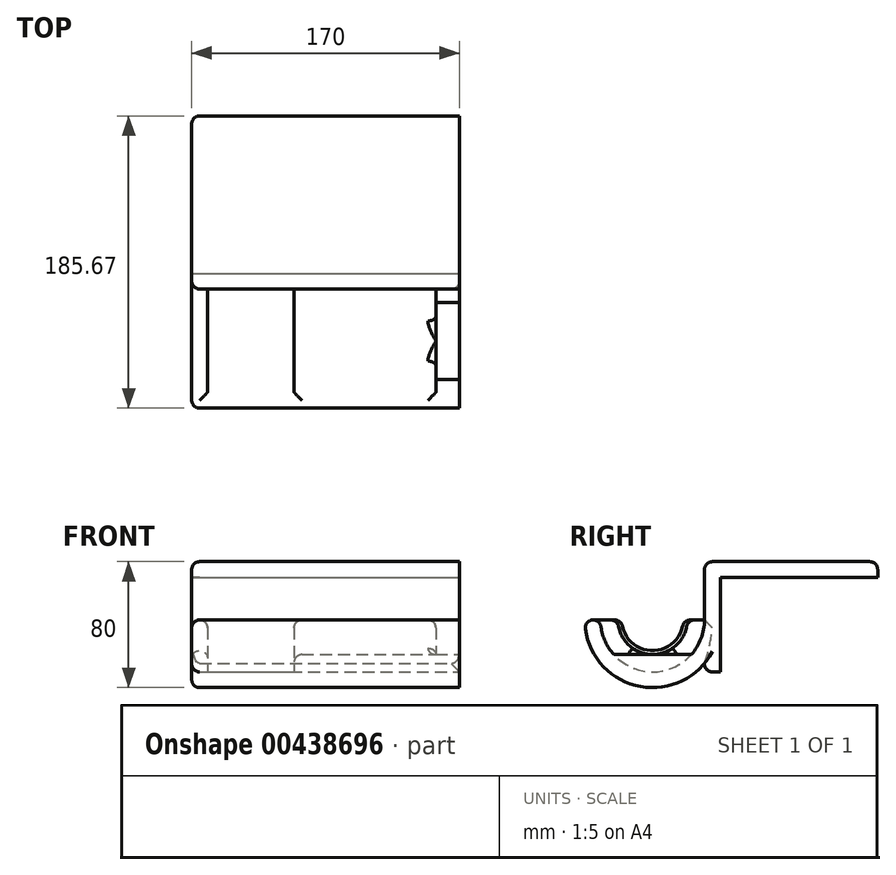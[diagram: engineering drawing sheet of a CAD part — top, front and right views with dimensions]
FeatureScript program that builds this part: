
annotation { "Feature Type Name" : "Feature", "Feature Type Description" : "" }
export const myFeature = defineFeature(function(context is Context, id is Id, definition is map)
    precondition{}
    {
        {
            var Q0;
            Q0=qCreatedBy(makeId("Front.planeOp"),FACE);
            var sketch = newSketch(context, id + "F0", { "sketchPlane" : qUnion([Q0])});
            skLineSegment(sketch, "E0.bottom", {"start": v(-170, 10) * mm, "end": v(170, 10) * mm});
            skLineSegment(sketch, "E0.top", {"start": v(-170, -60) * mm, "end": v(170, -60) * mm});
            skLineSegment(sketch, "E0.left", {"start": v(-170, 10) * mm, "end": v(-170, -60) * mm});
            skLineSegment(sketch, "E0.right", {"start": v(170, 10) * mm, "end": v(170, -60) * mm});
            skSolve(sketch);
        }
        {
            var Q0;
            Q0=qSketchRegion(id+"F0",true);
            extrude(context, id + "F1", {"entities" : qUnion([Q0]), "depth" : 10 * mm});
        }
        {
            var Q0;
            Q0=qCreatedBy(makeId("Top.planeOp"),FACE);
            var sketch = newSketch(context, id + "F2", { "sketchPlane" : qUnion([Q0])});
            skLineSegment(sketch, "E1.bottom", {"start": v(-170, 0) * mm, "end": v(170, 0) * mm});
            skLineSegment(sketch, "E1.top", {"start": v(-170, 100) * mm, "end": v(170, 100) * mm});
            skLineSegment(sketch, "E1.left", {"start": v(-170, 0) * mm, "end": v(-170, 100) * mm});
            skLineSegment(sketch, "E1.right", {"start": v(170, 0) * mm, "end": v(170, 100) * mm});
            skSolve(sketch);
        }
        {
            var Q0;
            Q0=qSketchRegion(id+"F2",true);
            extrude(context, id + "F3", {"entities" : qUnion([Q0]), "operationType" : NewBodyOperationType.ADD, "depth" : 10 * mm});
        }
        {
            var Q0;
            Q0=qCreatedBy(makeId("Top.planeOp"),FACE);
            cPlane(context, id + "F4", {"entities" : qUnion([Q0]), "cplaneType" : CPlaneType.OFFSET, "offset" : 27 * mm, "oppositeDirection" : true, "width" : 150 * mm, "height" : 150 * mm});
        }
        {
            var Q0;
            Q0=qCreatedBy(id+"F4.planeOp",FACE);
            var sketch = newSketch(context, id + "F5", { "sketchPlane" : qUnion([Q0])});
            skLineSegment(sketch, "E2", {"start": v(-170, 0) * mm, "end": v(-170, -43) * mm});
            skLineSegment(sketch, "E3", {"start": v(-170, -43) * mm, "end": v(-160, -43) * mm});
            skLineSegment(sketch, "E4", {"start": v(-160, -43) * mm, "end": v(-160, -10) * mm});
            skLineSegment(sketch, "E5", {"start": v(-160, -10) * mm, "end": v(-105, -10) * mm});
            skLineSegment(sketch, "E6", {"start": v(-105, -10) * mm, "end": v(-105, -21) * mm});
            skLineSegment(sketch, "E7", {"start": v(-105, -21) * mm, "end": v(-15, -21) * mm});
            skLineSegment(sketch, "E8", {"start": v(-15, -21) * mm, "end": v(-15, -10) * mm});
            skLineSegment(sketch, "E9", {"start": v(-15, -10) * mm, "end": v(52.5, -10) * mm});
            skLineSegment(sketch, "E10", {"start": v(52.5, -10) * mm, "end": v(52.5, -21) * mm});
            skLineSegment(sketch, "E11", {"start": v(52.5, -21) * mm, "end": v(105, -21) * mm});
            skLineSegment(sketch, "E12", {"start": v(105, -21) * mm, "end": v(105, -10) * mm});
            skLineSegment(sketch, "E13", {"start": v(105, -10) * mm, "end": v(160, -10) * mm});
            skLineSegment(sketch, "E14", {"start": v(160, -10) * mm, "end": v(160, -43) * mm});
            skLineSegment(sketch, "E15", {"start": v(160, -43) * mm, "end": v(170, -43) * mm});
            skLineSegment(sketch, "E16", {"start": v(170, -43) * mm, "end": v(170, 0) * mm});
            skLineSegment(sketch, "E17", {"start": v(170, 0) * mm, "end": v(-170, 0) * mm});
            skSolve(sketch);
        }
        {
            var Q0;
            Q0=qCreatedBy(id+"F4.planeOp",FACE);
            var sketch = newSketch(context, id + "F6", { "sketchPlane" : qUnion([Q0])});
            skLineSegment(sketch, "E18", {"start": v(170, -43) * mm, "end": v(-170, -43) * mm});
            skSolve(sketch);
        }
        {
            var Q0;
            Q0=qSketchRegion(id+"F5",true);
            var Q1;
            Q1=sQuery(id+"F6.wireOp",EDGE,"E18");
            revolve(context, id + "F7", {"operationType" : NewBodyOperationType.ADD, "entities" : qUnion([Q0]), "axis" : qUnion([Q1]), "revolveType" : RevolveType.ONE_DIRECTION, "angle" : 180 * degree});
        }
        {
            var Q0;
            Q0=qCreatedBy(makeId("Right.planeOp"),FACE);
            var sketch = newSketch(context, id + "F8", { "sketchPlane" : qUnion([Q0])});
            skCircle(sketch, "E19", {"center": v(-43, -27) * mm, "radius": 19.5 * mm});
            skSolve(sketch);
        }
        {
            var Q0;
            Q0=makeQuery(id+"F8.imprint","IMPRINT",FACE,{"disambiguationData":[TD([[makeQuery(id+"F8.imprint","IMPRINT",EDGE,{"derivedFrom":sQuery(id+"F8.wireOp",EDGE,"E19")}),1.0]])]});
            extrude(context, id + "F9", {"entities" : qUnion([Q0]), "operationType" : NewBodyOperationType.REMOVE, "endBound" : BoundingType.THROUGH_ALL, "depth" : 25 * mm});
        }
        {
            var Q0;
            Q0=qSketchRegion(id+"F8",true);
            extrude(context, id + "F10", {"entities" : qUnion([Q0]), "operationType" : NewBodyOperationType.REMOVE, "endBound" : BoundingType.THROUGH_ALL, "oppositeDirection" : true, "depth" : 25 * mm});
        }
        {
            var Q0;
            Q0=qCreatedBy(id+"F4.planeOp",FACE);
            cPlane(context, id + "F11", {"entities" : qUnion([Q0]), "cplaneType" : CPlaneType.OFFSET, "offset" : 22 * mm, "oppositeDirection" : true, "width" : 150 * mm, "height" : 150 * mm});
        }
        {
            var Q0;
            Q0=qCreatedBy(id+"F11.planeOp",FACE);
            var sketch = newSketch(context, id + "F12", { "sketchPlane" : qUnion([Q0])});
            skLineSegment(sketch, "E20.bottom", {"start": v(-15, -10) * mm, "end": v(52.5, -10) * mm});
            skLineSegment(sketch, "E20.top", {"start": v(-15, -76) * mm, "end": v(52.5, -76) * mm});
            skLineSegment(sketch, "E20.left", {"start": v(-15, -10) * mm, "end": v(-15, -76) * mm});
            skLineSegment(sketch, "E20.right", {"start": v(52.5, -10) * mm, "end": v(52.5, -76) * mm});
            skSolve(sketch);
        }
        {
            var Q0;
            Q0=makeQuery(id+"F12.imprint","IMPRINT",FACE,{"disambiguationData":[TD([[makeQuery(id+"F12.imprint","IMPRINT",EDGE,{"derivedFrom":sQuery(id+"F12.wireOp",EDGE,"E20.bottom")}),-1.0]])]});
            extrude(context, id + "F13", {"entities" : qUnion([Q0]), "operationType" : NewBodyOperationType.ADD, "oppositeDirection" : true, "depth" : 25 * mm});
        }
        {
            var Q0;
            Q0=makeQuery(id+"F13.opExtrude","SWEPT_FACE",FACE,{"disambiguationData":[OSD([sQuery(id+"F12.wireOp",EDGE,"E20.right")])]});
            var sketch = newSketch(context, id + "F14", { "sketchPlane" : qUnion([Q0])});
            skLineSegment(sketch, "E21", {"start": v(-76, -54.57) * mm, "end": v(-76, -74) * mm});
            skLineSegment(sketch, "E22", {"start": v(-76, -74) * mm, "end": v(-10, -74) * mm});
            skLineSegment(sketch, "E23", {"start": v(-10, -74) * mm, "end": v(-10, -54.57) * mm});
            skArc(sketch, "E24", {"start": v(-76, -54.57) * mm, "mid": v(-43, -70) * mm, "end": v(-10, -54.57) * mm});
            skSolve(sketch);
        }
        {
            var Q0;
            Q0=qSketchRegion(id+"F14",true);
            extrude(context, id + "F15", {"entities" : qUnion([Q0]), "operationType" : NewBodyOperationType.REMOVE, "endBound" : BoundingType.THROUGH_ALL, "oppositeDirection" : true, "depth" : 25 * mm});
        }
        {
            var Q0;
            Q0=qCreatedBy(makeId("Front.planeOp"),FACE);
            var sketch = newSketch(context, id + "F16", { "sketchPlane" : qUnion([Q0])});
            skLineSegment(sketch, "E25.bottom", {"start": v(0, 100) * mm, "end": v(200, 100) * mm});
            skLineSegment(sketch, "E25.top", {"start": v(0, -100) * mm, "end": v(200, -100) * mm});
            skLineSegment(sketch, "E25.left", {"start": v(0, 100) * mm, "end": v(0, -100) * mm});
            skLineSegment(sketch, "E25.right", {"start": v(200, 100) * mm, "end": v(200, -100) * mm});
            skSolve(sketch);
        }
        {
            var Q0;
            Q0 = qSketchRegion(id + "F16", true);
            extrude(context, id + "F17", {"entities" : qUnion([Q0]), "operationType" : NewBodyOperationType.REMOVE, "endBound" : BoundingType.THROUGH_ALL, "oppositeDirection" : true, "depth" : 25 * mm});
        }
        {
            var Q0;
            Q0 = qSketchRegion(id + "F16", true);
            extrude(context, id + "F18", {"entities" : qUnion([Q0]), "operationType" : NewBodyOperationType.REMOVE, "endBound" : BoundingType.THROUGH_ALL, "depth" : 25 * mm});
        }
        {
            var Q0;
            Q0=makeQuery(id+"F7.opRevolve","CAP_EDGE",EDGE,{"disambiguationData":[OSD([sQuery(id+"F5.wireOp",EDGE,"E17")])],"isStart":false});
            var Q1;
            Q1=makeQuery(id+"F7.opRevolve","CAP_EDGE",EDGE,{"disambiguationData":[OSD([sQuery(id+"F5.wireOp",EDGE,"E9")])],"isStart":false});
            var Q2;
            Q2=makeQuery(id+"F13.boolean.opBoolean","SPLIT",EDGE,{"disambiguationData":[OD(1.0)],"derivedFrom":makeQuery(id+"F7.opRevolve","SWEPT_EDGE",EDGE,{"disambiguationData":[OSD([sQuery(id+"F5.wireOp",EDGE,"E7"),sQuery(id+"F5.wireOp",EDGE,"E8")])]})});
            var Q3;
            Q3=makeQuery(id+"F7.opRevolve","CAP_EDGE",EDGE,{"disambiguationData":[OSD([sQuery(id+"F5.wireOp",EDGE,"E8")])],"isStart":true});
            var Q4;
            Q4=makeQuery(id+"F7.opRevolve","CAP_EDGE",EDGE,{"disambiguationData":[OSD([sQuery(id+"F5.wireOp",EDGE,"E7")])],"isStart":true});
            var Q5;
            Q5=makeQuery(id+"F7.opRevolve","CAP_EDGE",EDGE,{"disambiguationData":[OSD([sQuery(id+"F5.wireOp",EDGE,"E7")])],"isStart":false});
            var Q6;
            Q6=makeQuery(id+"F7.opRevolve","CAP_EDGE",EDGE,{"disambiguationData":[OSD([sQuery(id+"F5.wireOp",EDGE,"E8")])],"isStart":false});
            var Q7;
            Q7=makeQuery(id+"F7.opRevolve","CAP_EDGE",EDGE,{"disambiguationData":[OSD([sQuery(id+"F5.wireOp",EDGE,"E6")])],"isStart":false});
            var Q8;
            Q8=makeQuery(id+"F7.opRevolve","CAP_EDGE",EDGE,{"disambiguationData":[OSD([sQuery(id+"F5.wireOp",EDGE,"E6")])],"isStart":true});
            var Q9;
            Q9=makeQuery(id+"F7.opRevolve","SWEPT_EDGE",EDGE,{"disambiguationData":[OSD([sQuery(id+"F5.wireOp",EDGE,"E6"),sQuery(id+"F5.wireOp",EDGE,"E7")])]});
            var Q10;
            Q10=makeQuery(id+"F10.boolean.opBoolean","INTERSECT",EDGE,{"derivedFrom":[makeQuery(id+"F7.opRevolve","SWEPT_FACE",FACE,{"disambiguationData":[OSD([sQuery(id+"F5.wireOp",EDGE,"E4")])]}),makeQuery(id+"F10.opExtrude","SWEPT_FACE",FACE,{"disambiguationData":[OSD([sQuery(id+"F8.wireOp",EDGE,"E19")])]})]});
            var Q11;
            Q11=makeQuery(id+"F10.boolean.opBoolean","INTERSECT",EDGE,{"derivedFrom":[makeQuery(id+"F7.boolean.opBoolean","MERGE",FACE,{"derivedFrom":[makeQuery(id+"F3.boolean.opBoolean","MERGE",FACE,{"derivedFrom":[makeQuery(id+"F1.opExtrude","SWEPT_FACE",FACE,{"disambiguationData":[OSD([sQuery(id+"F0.wireOp",EDGE,"E0.left")])]}),makeQuery(id+"F3.opExtrude","SWEPT_FACE",FACE,{"disambiguationData":[OSD([sQuery(id+"F2.wireOp",EDGE,"E1.left")])]})]}),makeQuery(id+"F7.opRevolve","SWEPT_FACE",FACE,{"disambiguationData":[OSD([sQuery(id+"F5.wireOp",EDGE,"E2")])]})]}),makeQuery(id+"F10.opExtrude","SWEPT_FACE",FACE,{"disambiguationData":[OSD([sQuery(id+"F8.wireOp",EDGE,"E19")])]})]});
            var Q12;
            {var subQ0=sQuery(id+"F5.wireOp",EDGE,"E17");var subQ1=sQuery(id+"F5.wireOp",EDGE,"E2");Q12=makeQuery(id+"F10.boolean.opBoolean","SPLIT",EDGE,{"disambiguationData":[TD([makeQuery(id+"F7.opRevolve","SWEPT_FACE",FACE,{"disambiguationData":[OSD([subQ0])]})])],"derivedFrom":makeQuery(id+"F7.opRevolve","CAP_EDGE",EDGE,{"disambiguationData":[OSD([subQ1])],"isStart":false})});}
            var Q13;
            {var subQ0=sQuery(id+"F5.wireOp",EDGE,"E5");var subQ1=sQuery(id+"F5.wireOp",EDGE,"E4");Q13=makeQuery(id+"F10.boolean.opBoolean","SPLIT",EDGE,{"disambiguationData":[TD([makeQuery(id+"F7.opRevolve","CAP_FACE",FACE,{"disambiguationData":[OSD([sQuery(id+"F5.wireOp",EDGE,"E2"),sQuery(id+"F5.wireOp",EDGE,"E3"),subQ1,subQ0,sQuery(id+"F5.wireOp",EDGE,"E6"),sQuery(id+"F5.wireOp",EDGE,"E7"),sQuery(id+"F5.wireOp",EDGE,"E8"),sQuery(id+"F5.wireOp",EDGE,"E9"),sQuery(id+"F5.wireOp",EDGE,"E10"),sQuery(id+"F5.wireOp",EDGE,"E11"),sQuery(id+"F5.wireOp",EDGE,"E12"),sQuery(id+"F5.wireOp",EDGE,"E13"),sQuery(id+"F5.wireOp",EDGE,"E14"),sQuery(id+"F5.wireOp",EDGE,"E15"),sQuery(id+"F5.wireOp",EDGE,"E16"),sQuery(id+"F5.wireOp",EDGE,"E17")])],"isStart":false}),makeQuery(id+"F7.opRevolve","SWEPT_FACE",FACE,{"disambiguationData":[OSD([subQ1])]}),makeQuery(id+"F7.opRevolve","SWEPT_FACE",FACE,{"disambiguationData":[OSD([subQ0])]}),makeQuery(id+"F10.opExtrude","SWEPT_FACE",FACE,{"disambiguationData":[OSD([sQuery(id+"F8.wireOp",EDGE,"E19")])]})])],"derivedFrom":makeQuery(id+"F7.opRevolve","CAP_EDGE",EDGE,{"disambiguationData":[OSD([subQ1])],"isStart":false})});}
            var Q14;
            {var subQ0=sQuery(id+"F5.wireOp",EDGE,"E4");var subQ1=sQuery(id+"F5.wireOp",EDGE,"E5");Q14=makeQuery(id+"F10.boolean.opBoolean","SPLIT",EDGE,{"disambiguationData":[TD([makeQuery(id+"F1.opExtrude","CAP_FACE",FACE,{"disambiguationData":[OSD([sQuery(id+"F0.wireOp",EDGE,"E0.bottom"),sQuery(id+"F0.wireOp",EDGE,"E0.top"),sQuery(id+"F0.wireOp",EDGE,"E0.left"),sQuery(id+"F0.wireOp",EDGE,"E0.right")])],"isStart":false}),makeQuery(id+"F7.opRevolve","CAP_FACE",FACE,{"disambiguationData":[OSD([sQuery(id+"F5.wireOp",EDGE,"E2"),sQuery(id+"F5.wireOp",EDGE,"E3"),subQ0,subQ1,sQuery(id+"F5.wireOp",EDGE,"E6"),sQuery(id+"F5.wireOp",EDGE,"E7"),sQuery(id+"F5.wireOp",EDGE,"E8"),sQuery(id+"F5.wireOp",EDGE,"E9"),sQuery(id+"F5.wireOp",EDGE,"E10"),sQuery(id+"F5.wireOp",EDGE,"E11"),sQuery(id+"F5.wireOp",EDGE,"E12"),sQuery(id+"F5.wireOp",EDGE,"E13"),sQuery(id+"F5.wireOp",EDGE,"E14"),sQuery(id+"F5.wireOp",EDGE,"E15"),sQuery(id+"F5.wireOp",EDGE,"E16"),sQuery(id+"F5.wireOp",EDGE,"E17")])],"isStart":false}),makeQuery(id+"F7.opRevolve","SWEPT_FACE",FACE,{"disambiguationData":[OSD([subQ0])]}),makeQuery(id+"F7.opRevolve","SWEPT_FACE",FACE,{"disambiguationData":[OSD([subQ1])]}),makeQuery(id+"F10.opExtrude","SWEPT_FACE",FACE,{"disambiguationData":[OSD([sQuery(id+"F8.wireOp",EDGE,"E19")])]})])],"derivedFrom":makeQuery(id+"F7.opRevolve","CAP_EDGE",EDGE,{"disambiguationData":[OSD([subQ0])],"isStart":false})});}
            var Q15;
            {var subQ0=sQuery(id+"F5.wireOp",EDGE,"E2");var subQ1=sQuery(id+"F0.wireOp",EDGE,"E0.left");Q15=makeQuery(id+"F10.boolean.opBoolean","SPLIT",EDGE,{"disambiguationData":[TD([makeQuery(id+"F1.opExtrude","CAP_FACE",FACE,{"disambiguationData":[OSD([sQuery(id+"F0.wireOp",EDGE,"E0.bottom"),sQuery(id+"F0.wireOp",EDGE,"E0.top"),subQ1,sQuery(id+"F0.wireOp",EDGE,"E0.right")])],"isStart":false})])],"derivedFrom":makeQuery(id+"F7.opRevolve","CAP_EDGE",EDGE,{"disambiguationData":[OSD([subQ0])],"isStart":false})});}
            var Q16;
            Q16=makeQuery(id+"F7.opRevolve","CAP_EDGE",EDGE,{"disambiguationData":[OSD([sQuery(id+"F5.wireOp",EDGE,"E5")])],"isStart":false});
            var Q17;
            {var subQ0=sQuery(id+"F8.wireOp",EDGE,"E19");var subQ1=sQuery(id+"F5.wireOp",EDGE,"E7");var subQ2=makeQuery(id+"F7.opRevolve","SWEPT_FACE",FACE,{"disambiguationData":[OSD([subQ1])]});var subQ3=sQuery(id+"F5.wireOp",EDGE,"E6");var subQ4=makeQuery(id+"F7.opRevolve","SWEPT_FACE",FACE,{"disambiguationData":[OSD([subQ3])]});var subQ5=sQuery(id+"F5.wireOp",EDGE,"E2");var subQ6=makeQuery(id+"F7.opRevolve","SWEPT_FACE",FACE,{"disambiguationData":[OSD([subQ5])]});var subQ7=sQuery(id+"F5.wireOp",EDGE,"E5");var subQ8=makeQuery(id+"F7.opRevolve","SWEPT_FACE",FACE,{"disambiguationData":[OSD([subQ7])]});var subQ9=makeQuery(id+"F3.opExtrude","SWEPT_FACE",FACE,{"disambiguationData":[OSD([sQuery(id+"F2.wireOp",EDGE,"E1.right")])]});var subQ10=sQuery(id+"F0.wireOp",EDGE,"E0.right");var subQ11=sQuery(id+"F0.wireOp",EDGE,"E0.left");var subQ12=makeQuery(id+"F1.opExtrude","CAP_FACE",FACE,{"disambiguationData":[OSD([sQuery(id+"F0.wireOp",EDGE,"E0.bottom"),sQuery(id+"F0.wireOp",EDGE,"E0.top"),subQ11,subQ10])],"isStart":false});var subQ13=sQuery(id+"F5.wireOp",EDGE,"E16");var subQ14=makeQuery(id+"F7.opRevolve","SWEPT_FACE",FACE,{"disambiguationData":[OSD([subQ13])]});var subQ15=makeQuery(id+"F1.opExtrude","SWEPT_FACE",FACE,{"disambiguationData":[OSD([subQ11])]});var subQ16=sQuery(id+"F5.wireOp",EDGE,"E4");var subQ17=makeQuery(id+"F7.opRevolve","SWEPT_FACE",FACE,{"disambiguationData":[OSD([subQ16])]});var subQ18=makeQuery(id+"F3.opExtrude","SWEPT_FACE",FACE,{"disambiguationData":[OSD([sQuery(id+"F2.wireOp",EDGE,"E1.left")])]});var subQ19=makeQuery(id+"F1.opExtrude","SWEPT_FACE",FACE,{"disambiguationData":[OSD([subQ10])]});var subQ20=sQuery(id+"F5.wireOp",EDGE,"E8");var subQ21=makeQuery(id+"F7.opRevolve","SWEPT_FACE",FACE,{"disambiguationData":[OSD([subQ20])]});var subQ22=sQuery(id+"F5.wireOp",EDGE,"E9");var subQ23=makeQuery(id+"F7.opRevolve","SWEPT_FACE",FACE,{"disambiguationData":[OSD([subQ22])]});var subQ24=sQuery(id+"F5.wireOp",EDGE,"E10");var subQ25=makeQuery(id+"F7.opRevolve","SWEPT_FACE",FACE,{"disambiguationData":[OSD([subQ24])]});var subQ26=sQuery(id+"F5.wireOp",EDGE,"E11");var subQ27=makeQuery(id+"F7.opRevolve","SWEPT_FACE",FACE,{"disambiguationData":[OSD([subQ26])]});var subQ28=sQuery(id+"F5.wireOp",EDGE,"E12");var subQ29=makeQuery(id+"F7.opRevolve","SWEPT_FACE",FACE,{"disambiguationData":[OSD([subQ28])]});var subQ30=sQuery(id+"F5.wireOp",EDGE,"E13");var subQ31=makeQuery(id+"F7.opRevolve","SWEPT_FACE",FACE,{"disambiguationData":[OSD([subQ30])]});var subQ32=sQuery(id+"F5.wireOp",EDGE,"E14");var subQ33=makeQuery(id+"F7.opRevolve","SWEPT_FACE",FACE,{"disambiguationData":[OSD([subQ32])]});var subQ34=sQuery(id+"F5.wireOp",EDGE,"E17");var subQ35=makeQuery(id+"F7.opRevolve","SWEPT_FACE",FACE,{"disambiguationData":[OSD([subQ34])]});Q17=makeQuery(id+"F10.boolean.opBoolean","INTERSECT",EDGE,{"disambiguationData":[OD(0.0)],"derivedFrom":[makeQuery(id+"F9.boolean.opBoolean","SPLIT",FACE,{"disambiguationData":[TD([subQ12,subQ15,subQ19,subQ18,subQ9,subQ6,subQ17,subQ8,subQ4,subQ2,subQ21,subQ23,subQ25,subQ27,subQ29,subQ31,subQ33,subQ14,subQ35,makeQuery(id+"F9.opExtrude","SWEPT_FACE",FACE,{"disambiguationData":[OSD([subQ0])]})])],"derivedFrom":makeQuery(id+"F7.boolean.opBoolean","SPLIT",FACE,{"disambiguationData":[TD([subQ12,subQ15,subQ19,subQ18,subQ9,subQ6,subQ17,subQ8,subQ4,subQ2,subQ21,subQ23,subQ25,subQ27,subQ29,subQ31,subQ33,subQ14,subQ35])],"derivedFrom":makeQuery(id+"F7.opRevolve","CAP_FACE",FACE,{"disambiguationData":[OSD([subQ5,sQuery(id+"F5.wireOp",EDGE,"E3"),subQ16,subQ7,subQ3,subQ1,subQ20,subQ22,subQ24,subQ26,subQ28,subQ30,subQ32,sQuery(id+"F5.wireOp",EDGE,"E15"),subQ13,subQ34])],"isStart":false})})}),makeQuery(id+"F10.opExtrude","SWEPT_FACE",FACE,{"disambiguationData":[OSD([subQ0])]})]});}
            var Q18;
            {var subQ0=sQuery(id+"F0.wireOp",EDGE,"E0.top");var subQ1=makeQuery(id+"F1.opExtrude","SWEPT_FACE",FACE,{"disambiguationData":[OSD([subQ0])]});var subQ2=makeQuery(id+"F13.opExtrude","SWEPT_FACE",FACE,{"disambiguationData":[OSD([sQuery(id+"F12.wireOp",EDGE,"E20.bottom")])]});var subQ3=makeQuery(id+"F1.opExtrude","CAP_EDGE",EDGE,{"disambiguationData":[OSD([subQ0])],"isStart":false});var subQ4=sQuery(id+"F0.wireOp",EDGE,"E0.right");var subQ5=sQuery(id+"F0.wireOp",EDGE,"E0.left");var subQ6=makeQuery(id+"F1.opExtrude","CAP_FACE",FACE,{"disambiguationData":[OSD([sQuery(id+"F0.wireOp",EDGE,"E0.bottom"),subQ0,subQ5,subQ4])],"isStart":false});Q18=makeQuery(id+"F15.boolean.opBoolean","MERGE",EDGE,{"derivedFrom":[makeQuery(id+"F13.boolean.opBoolean","SPLIT",EDGE,{"disambiguationData":[topologyDisambiguationEdgeConnected([subQ6,subQ1]),TD([makeQuery(id+"F1.opExtrude","SWEPT_FACE",FACE,{"disambiguationData":[OSD([subQ5])]})])],"derivedFrom":subQ3}),makeQuery(id+"F13.boolean.opBoolean","SPLIT",EDGE,{"disambiguationData":[topologyDisambiguationEdgeConnected([subQ6,subQ1]),TD([makeQuery(id+"F1.opExtrude","SWEPT_FACE",FACE,{"disambiguationData":[OSD([subQ4])]})])],"derivedFrom":subQ3}),makeQuery(id+"F13.boolean.opBoolean","SPLIT",EDGE,{"disambiguationData":[topologyDisambiguationEdgeConnected([subQ1,subQ2])],"derivedFrom":subQ3})]});}
            var Q19;
            {var subQ0=sQuery(id+"F0.wireOp",EDGE,"E0.left");var subQ1=sQuery(id+"F0.wireOp",EDGE,"E0.top");Q19=makeQuery(id+"F7.boolean.opBoolean","SPLIT",EDGE,{"disambiguationData":[TD([makeQuery(id+"F1.opExtrude","SWEPT_FACE",FACE,{"disambiguationData":[OSD([subQ1])]})])],"derivedFrom":makeQuery(id+"F1.opExtrude","CAP_EDGE",EDGE,{"disambiguationData":[OSD([subQ0])],"isStart":false})});}
            var Q20;
            {var subQ1=sQuery(id+"F0.wireOp",EDGE,"E0.right");var subQ2=makeQuery(id+"F1.opExtrude","SWEPT_FACE",FACE,{"disambiguationData":[OSD([subQ1])]});var subQ5=sQuery(id+"F0.wireOp",EDGE,"E0.top");var subQ6=makeQuery(id+"F1.opExtrude","SWEPT_FACE",FACE,{"disambiguationData":[OSD([subQ5])]});var subQ9=sQuery(id+"F0.wireOp",EDGE,"E0.left");var subQ10=makeQuery(id+"F1.opExtrude","SWEPT_FACE",FACE,{"disambiguationData":[OSD([subQ9])]});var subQ12=makeQuery(id+"F7.boolean.opBoolean","SPLIT",FACE,{"disambiguationData":[TD([subQ6])],"derivedFrom":makeQuery(id+"F1.opExtrude","CAP_FACE",FACE,{"disambiguationData":[OSD([sQuery(id+"F0.wireOp",EDGE,"E0.bottom"),subQ5,subQ9,subQ1])],"isStart":false})});Q20=makeQuery(id+"F18.boolean.opBoolean","INTERSECT",EDGE,{"derivedFrom":[makeQuery(id+"F15.boolean.opBoolean","MERGE",FACE,{"derivedFrom":[makeQuery(id+"F13.boolean.opBoolean","SPLIT",FACE,{"disambiguationData":[TD([subQ10])],"derivedFrom":subQ12}),makeQuery(id+"F13.boolean.opBoolean","SPLIT",FACE,{"disambiguationData":[TD([subQ2])],"derivedFrom":subQ12}),makeQuery(id+"F15.opExtrude","SWEPT_FACE",FACE,{"disambiguationData":[OSD([sQuery(id+"F14.wireOp",EDGE,"E23")])]})]}),makeQuery(id+"F18.opExtrude","SWEPT_FACE",FACE,{"disambiguationData":[OSD([sQuery(id+"F16.wireOp",EDGE,"E25.left")])]})]});}
            var Q21;
            Q21=makeQuery(id+"F1.opExtrude","SWEPT_EDGE",EDGE,{"disambiguationData":[OSD([sQuery(id+"F0.wireOp",EDGE,"E0.top"),sQuery(id+"F0.wireOp",EDGE,"E0.left")])]});
            var Q22;
            Q22=makeQuery(id+"F7.opRevolve","SWEPT_EDGE",EDGE,{"disambiguationData":[OSD([sQuery(id+"F5.wireOp",EDGE,"E2"),sQuery(id+"F5.wireOp",EDGE,"E17")])]});
            var Q23;
            Q23=makeQuery(id+"F13.boolean.opBoolean","SPLIT",EDGE,{"disambiguationData":[OD(0.0)],"derivedFrom":makeQuery(id+"F7.opRevolve","SWEPT_EDGE",EDGE,{"disambiguationData":[OSD([sQuery(id+"F5.wireOp",EDGE,"E7"),sQuery(id+"F5.wireOp",EDGE,"E8")])]})});
            var Q24;
            {var subQ0=sQuery(id+"F0.wireOp",EDGE,"E0.left");var subQ2=sQuery(id+"F0.wireOp",EDGE,"E0.bottom");Q24=makeQuery(id+"F7.boolean.opBoolean","SPLIT",EDGE,{"disambiguationData":[TD([makeQuery(id+"F1.opExtrude","SWEPT_FACE",FACE,{"disambiguationData":[OSD([subQ2])]})])],"derivedFrom":makeQuery(id+"F1.opExtrude","CAP_EDGE",EDGE,{"disambiguationData":[OSD([subQ0])],"isStart":false})});}
            var Q25;
            Q25=makeQuery(id+"F3.opExtrude","CAP_EDGE",EDGE,{"disambiguationData":[OSD([sQuery(id+"F2.wireOp",EDGE,"E1.top")])],"isStart":false});
            var Q26;
            Q26=makeQuery(id+"F3.boolean.opBoolean","MERGE",EDGE,{"derivedFrom":[makeQuery(id+"F1.opExtrude","SWEPT_EDGE",EDGE,{"disambiguationData":[OSD([sQuery(id+"F0.wireOp",EDGE,"E0.bottom"),sQuery(id+"F0.wireOp",EDGE,"E0.left")])]}),makeQuery(id+"F3.opExtrude","CAP_EDGE",EDGE,{"disambiguationData":[OSD([sQuery(id+"F2.wireOp",EDGE,"E1.left")])],"isStart":false})]});
            var Q27;
            Q27=makeQuery(id+"F3.opExtrude","SWEPT_EDGE",EDGE,{"disambiguationData":[OSD([sQuery(id+"F2.wireOp",EDGE,"E1.top"),sQuery(id+"F2.wireOp",EDGE,"E1.left")])]});
            var Q28;
            {var subQ0=sQuery(id+"F8.wireOp",EDGE,"E19");var subQ1=sQuery(id+"F5.wireOp",EDGE,"E7");var subQ2=makeQuery(id+"F7.opRevolve","SWEPT_FACE",FACE,{"disambiguationData":[OSD([subQ1])]});var subQ3=sQuery(id+"F5.wireOp",EDGE,"E6");var subQ4=makeQuery(id+"F7.opRevolve","SWEPT_FACE",FACE,{"disambiguationData":[OSD([subQ3])]});var subQ5=sQuery(id+"F5.wireOp",EDGE,"E2");var subQ6=makeQuery(id+"F7.opRevolve","SWEPT_FACE",FACE,{"disambiguationData":[OSD([subQ5])]});var subQ7=sQuery(id+"F5.wireOp",EDGE,"E5");var subQ8=makeQuery(id+"F7.opRevolve","SWEPT_FACE",FACE,{"disambiguationData":[OSD([subQ7])]});var subQ9=makeQuery(id+"F3.opExtrude","SWEPT_FACE",FACE,{"disambiguationData":[OSD([sQuery(id+"F2.wireOp",EDGE,"E1.right")])]});var subQ10=sQuery(id+"F0.wireOp",EDGE,"E0.right");var subQ11=sQuery(id+"F0.wireOp",EDGE,"E0.left");var subQ12=makeQuery(id+"F1.opExtrude","CAP_FACE",FACE,{"disambiguationData":[OSD([sQuery(id+"F0.wireOp",EDGE,"E0.bottom"),sQuery(id+"F0.wireOp",EDGE,"E0.top"),subQ11,subQ10])],"isStart":false});var subQ13=sQuery(id+"F5.wireOp",EDGE,"E16");var subQ14=makeQuery(id+"F7.opRevolve","SWEPT_FACE",FACE,{"disambiguationData":[OSD([subQ13])]});var subQ15=makeQuery(id+"F1.opExtrude","SWEPT_FACE",FACE,{"disambiguationData":[OSD([subQ11])]});var subQ16=sQuery(id+"F5.wireOp",EDGE,"E4");var subQ17=makeQuery(id+"F7.opRevolve","SWEPT_FACE",FACE,{"disambiguationData":[OSD([subQ16])]});var subQ18=makeQuery(id+"F3.opExtrude","SWEPT_FACE",FACE,{"disambiguationData":[OSD([sQuery(id+"F2.wireOp",EDGE,"E1.left")])]});var subQ19=makeQuery(id+"F1.opExtrude","SWEPT_FACE",FACE,{"disambiguationData":[OSD([subQ10])]});var subQ20=sQuery(id+"F5.wireOp",EDGE,"E8");var subQ21=makeQuery(id+"F7.opRevolve","SWEPT_FACE",FACE,{"disambiguationData":[OSD([subQ20])]});var subQ22=sQuery(id+"F5.wireOp",EDGE,"E9");var subQ23=makeQuery(id+"F7.opRevolve","SWEPT_FACE",FACE,{"disambiguationData":[OSD([subQ22])]});var subQ24=sQuery(id+"F5.wireOp",EDGE,"E10");var subQ25=makeQuery(id+"F7.opRevolve","SWEPT_FACE",FACE,{"disambiguationData":[OSD([subQ24])]});var subQ26=sQuery(id+"F5.wireOp",EDGE,"E11");var subQ27=makeQuery(id+"F7.opRevolve","SWEPT_FACE",FACE,{"disambiguationData":[OSD([subQ26])]});var subQ28=sQuery(id+"F5.wireOp",EDGE,"E12");var subQ29=makeQuery(id+"F7.opRevolve","SWEPT_FACE",FACE,{"disambiguationData":[OSD([subQ28])]});var subQ30=sQuery(id+"F5.wireOp",EDGE,"E13");var subQ31=makeQuery(id+"F7.opRevolve","SWEPT_FACE",FACE,{"disambiguationData":[OSD([subQ30])]});var subQ32=sQuery(id+"F5.wireOp",EDGE,"E14");var subQ33=makeQuery(id+"F7.opRevolve","SWEPT_FACE",FACE,{"disambiguationData":[OSD([subQ32])]});var subQ34=sQuery(id+"F5.wireOp",EDGE,"E17");var subQ35=makeQuery(id+"F7.opRevolve","SWEPT_FACE",FACE,{"disambiguationData":[OSD([subQ34])]});Q28=makeQuery(id+"F10.boolean.opBoolean","INTERSECT",EDGE,{"disambiguationData":[OD(1.0)],"derivedFrom":[makeQuery(id+"F9.boolean.opBoolean","SPLIT",FACE,{"disambiguationData":[TD([subQ12,subQ15,subQ19,subQ18,subQ9,subQ6,subQ17,subQ8,subQ4,subQ2,subQ21,subQ23,subQ25,subQ27,subQ29,subQ31,subQ33,subQ14,subQ35,makeQuery(id+"F9.opExtrude","SWEPT_FACE",FACE,{"disambiguationData":[OSD([subQ0])]})])],"derivedFrom":makeQuery(id+"F7.boolean.opBoolean","SPLIT",FACE,{"disambiguationData":[TD([subQ12,subQ15,subQ19,subQ18,subQ9,subQ6,subQ17,subQ8,subQ4,subQ2,subQ21,subQ23,subQ25,subQ27,subQ29,subQ31,subQ33,subQ14,subQ35])],"derivedFrom":makeQuery(id+"F7.opRevolve","CAP_FACE",FACE,{"disambiguationData":[OSD([subQ5,sQuery(id+"F5.wireOp",EDGE,"E3"),subQ16,subQ7,subQ3,subQ1,subQ20,subQ22,subQ24,subQ26,subQ28,subQ30,subQ32,sQuery(id+"F5.wireOp",EDGE,"E15"),subQ13,subQ34])],"isStart":false})})}),makeQuery(id+"F10.opExtrude","SWEPT_FACE",FACE,{"disambiguationData":[OSD([subQ0])]})]});}
            var Q29;
            Q29=makeQuery(id+"F1.opExtrude","CAP_EDGE",EDGE,{"disambiguationData":[OSD([sQuery(id+"F0.wireOp",EDGE,"E0.bottom")])],"isStart":false});
            fillet(context, id + "F19", {"entities" : qUnion([Q0, Q1, Q2, Q3, Q4, Q5, Q6, Q7, Q8, Q9, Q10, Q11, Q12, Q13, Q14, Q15, Q16, Q17, Q18, Q19, Q20, Q21, Q22, Q23, Q24, Q25, Q26, Q27, Q28, Q29]), "radius" : 5 * mm, "tangentPropagation" : true, "allowEdgeOverflow" : false});
        }
    });
